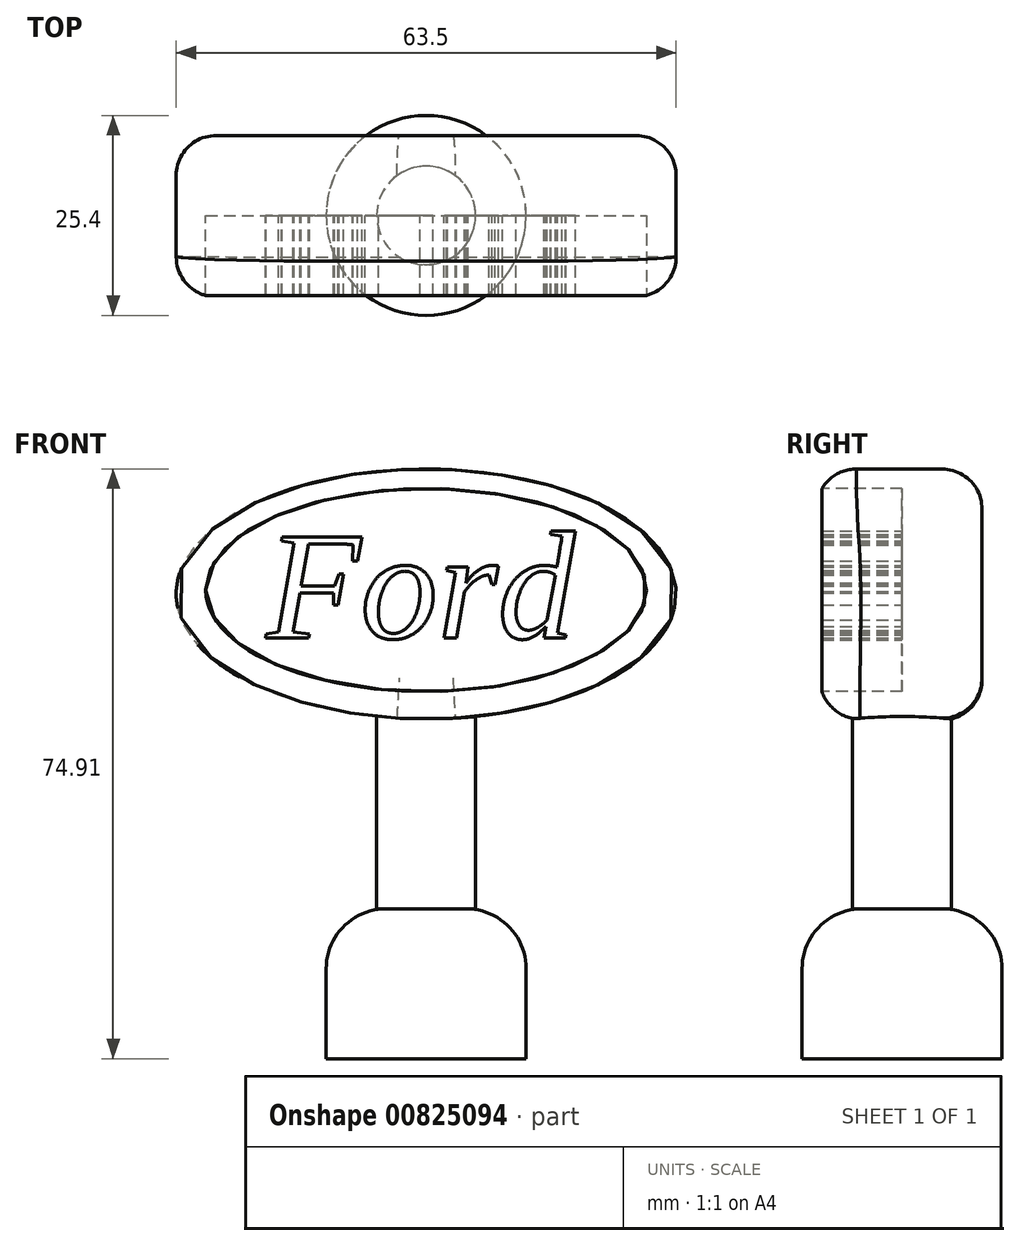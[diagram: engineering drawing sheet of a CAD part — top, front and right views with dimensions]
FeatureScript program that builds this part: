
annotation { "Feature Type Name" : "Feature", "Feature Type Description" : "" }
export const myFeature = defineFeature(function(context is Context, id is Id, definition is map)
    precondition{}
    {
        {
            var Q0;
            Q0=qCreatedBy(makeId("Top.planeOp"),FACE);
            var sketch = newSketch(context, id + "F0", { "sketchPlane" : qUnion([Q0])});
            skCircle(sketch, "E0", {"center": v(0, 0) * mm, "radius": 12.7 * mm});
            skSolve(sketch);
        }
        {
            var Q0;
            Q0=makeQuery(id+"F0.imprint","IMPRINT",FACE,{"disambiguationData":[TD([[makeQuery(id+"F0.imprint","IMPRINT",EDGE,{"derivedFrom":sQuery(id+"F0.wireOp",EDGE,"E0")}),1.0]])]});
            extrude(context, id + "F1", {"entities" : qUnion([Q0]), "depth" : 19.05 * mm, "offsetDistance" : 25.4 * mm});
        }
        {
            var Q0;
            Q0=makeQuery(id+"F1.opExtrude","CAP_FACE",FACE,{"disambiguationData":[OSD([sQuery(id+"F0.wireOp",EDGE,"E0")])],"isStart":false});
            var sketch = newSketch(context, id + "F2", { "sketchPlane" : qUnion([Q0])});
            skCircle(sketch, "E1", {"center": v(0, 0) * mm, "radius": 6.27 * mm});
            skSolve(sketch);
        }
        {
            var Q0;
            Q0=makeQuery(id+"F2.imprint","IMPRINT",FACE,{"disambiguationData":[TD([[makeQuery(id+"F2.imprint","IMPRINT",EDGE,{"derivedFrom":sQuery(id+"F2.wireOp",EDGE,"E1")}),1.0]])]});
            extrude(context, id + "F3", {"entities" : qUnion([Q0]), "depth" : 25.4 * mm, "offsetDistance" : 25.4 * mm});
        }
        {
            var Q0;
            Q0=qCreatedBy(makeId("Front.planeOp"),FACE);
            var sketch = newSketch(context, id + "F4", { "sketchPlane" : qUnion([Q0])});
            skEllipse(sketch, "E2", {"center": v(0, 59.03) * mm, "majorRadius": 31.75 * mm, "minorRadius": 15.88 * mm, "majorAxis": v(-1, 0)});
            skSolve(sketch);
        }
        {
            var Q0;
            Q0 = qSketchRegion(id + "F4", true);
            extrude(context, id + "F5", {"entities" : qUnion([Q0]), "operationType" : NewBodyOperationType.ADD, "endBound" : BoundingType.SYMMETRIC, "depth" : 20.32 * mm, "offsetDistance" : 25.4 * mm});
        }
        {
            var Q0;
            Q0=qCreatedBy(makeId("Front.planeOp"),FACE);
            var sketch = newSketch(context, id + "F6", { "sketchPlane" : qUnion([Q0])});
            skEllipse(sketch, "E3", {"center": v(0, 59.54) * mm, "majorRadius": 28 * mm, "minorRadius": 12.9 * mm, "majorAxis": v(-1, 0)});
            skSolve(sketch);
        }
        {
            var Q0;
            Q0=qCreatedBy(makeId("Front.planeOp"),FACE);
            var sketch = newSketch(context, id + "F7", { "sketchPlane" : qUnion([Q0])});
            skText(sketch, "E4", { "text": "Ford", "fontName": "Tinos-Italic.ttf"});
            const initialGuessF7  = {"E4": [-0.02032, 0.05342, 1, 0, 0.01413]};
            skSetInitialGuess(sketch, initialGuessF7);
            skSolve(sketch);
        }
        {
            var Q0;
            Q0 = qSketchRegion(id + "F6", true);
            var Q1;
            Q1=makeQuery(id+"F3.opExtrude","SWEPT_BODY",BODY,{"disambiguationData":[OSD([sQuery(id+"F2.wireOp",EDGE,"E1")])]});
            extrude(context, id + "F8", {"entities" : qUnion([Q0]), "operationType" : NewBodyOperationType.REMOVE, "endBound" : BoundingType.UP_TO_BODY, "depth" : 25.4 * mm, "endBoundEntityBody" : qUnion([Q1]), "offsetDistance" : 25.4 * mm});
        }
        {
            var Q0;
            Q0 = qSketchRegion(id + "F7", true);
            extrude(context, id + "F9", {"entities" : qUnion([Q0]), "operationType" : NewBodyOperationType.ADD, "depth" : 10.16 * mm, "offsetDistance" : 25.4 * mm});
        }
        {
            var Q0;
            Q0=makeQuery(id+"F5.opExtrude","CAP_EDGE",EDGE,{"disambiguationData":[OSD([sQuery(id+"F4.wireOp",EDGE,"E2")])],"isStart":false});
            var Q1;
            Q1=makeQuery(id+"F5.opExtrude","CAP_EDGE",EDGE,{"disambiguationData":[OSD([sQuery(id+"F4.wireOp",EDGE,"E2")])],"isStart":true});
            fillet(context, id + "F10", {"entities" : qUnion([Q0, Q1]), "radius" : 5.08 * mm, "tangentPropagation" : true, "allowEdgeOverflow" : false});
        }
        {
            var Q0;
            Q0=makeQuery(id+"F1.opExtrude","CAP_EDGE",EDGE,{"disambiguationData":[OSD([sQuery(id+"F0.wireOp",EDGE,"E0")])],"isStart":false});
            fillet(context, id + "F11", {"entities" : qUnion([Q0]), "radius" : 7.62 * mm, "tangentPropagation" : true, "allowEdgeOverflow" : false});
        }
    });
